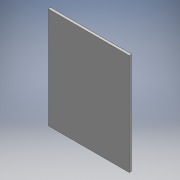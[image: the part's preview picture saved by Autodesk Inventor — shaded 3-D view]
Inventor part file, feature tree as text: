
AUTODESK INVENTOR PART (.ipt)
format: ipt  version: 2016 (Build 200138000, 138)  size: 85,504 bytes
history: native  units: mm
features: other x1, extrude x1, sketch x1
ambient origin geometry x8: Origin, YZ Plane, XZ Plane, XY Plane, X Axis, Y Axis, Z Axis, Center Point
bodies: Body1 (feature_tree)
feature tree (3):
  other  "Bryła1"
  extrude  "Wyciągnięcie proste1"  Depth=86.0mm
  sketch  "Szkic1"
